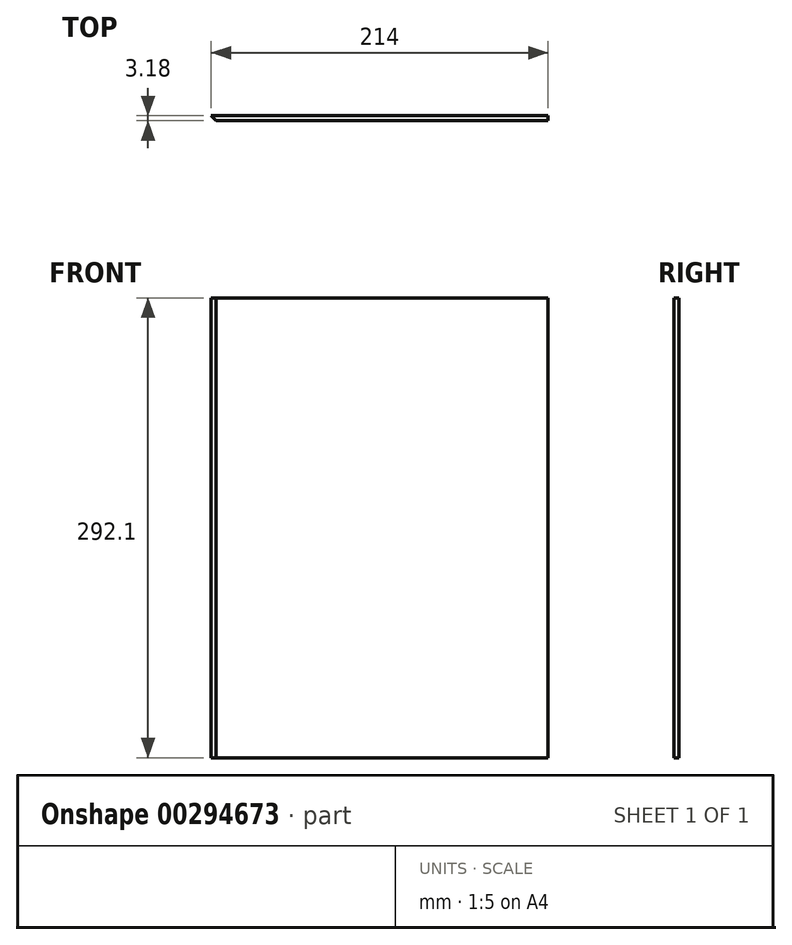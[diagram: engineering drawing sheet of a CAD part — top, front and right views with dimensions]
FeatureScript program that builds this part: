
annotation { "Feature Type Name" : "Feature", "Feature Type Description" : "" }
export const myFeature = defineFeature(function(context is Context, id is Id, definition is map)
    precondition{}
    {
        {
            var Q0;
            Q0=qCreatedBy(makeId("Front.planeOp"),FACE);
            var sketch = newSketch(context, id + "F0", { "sketchPlane" : qUnion([Q0])});
            skLineSegment(sketch, "E0.bottom", {"start": v(-107.95, 146.05) * mm, "end": v(107.95, 146.05) * mm});
            skLineSegment(sketch, "E0.top", {"start": v(-107.95, -146.05) * mm, "end": v(107.95, -146.05) * mm});
            skLineSegment(sketch, "E0.left", {"start": v(-107.95, 146.05) * mm, "end": v(-107.95, -146.05) * mm});
            skLineSegment(sketch, "E0.right", {"start": v(107.95, 146.05) * mm, "end": v(107.95, -146.05) * mm});
            skPoint(sketch, "E0.middle", {"position": v(0, 0) * mm});
            skSolve(sketch);
        }
        {
            var Q0;
            Q0=makeQuery(id+"F0.imprint","IMPRINT",FACE,{"disambiguationData":[TD([[makeQuery(id+"F0.imprint","IMPRINT",EDGE,{"derivedFrom":sQuery(id+"F0.wireOp",EDGE,"E0.bottom")}),-1.0]])]});
            extrude(context, id + "F1", {"entities" : qUnion([Q0]), "endBound" : BoundingType.SYMMETRIC, "depth" : 3.17 * mm});
        }
        {
            var Q0;
            Q0=makeQuery(id+"F1.opExtrude","CAP_EDGE",EDGE,{"disambiguationData":[OSD([sQuery(id+"F0.wireOp",EDGE,"E0.left")])],"isStart":false});
            chamfer(context, id + "F2", {"entities" : qUnion([Q0]), "width" : 5.08 * mm, "tangentPropagation" : true});
        }
    });
